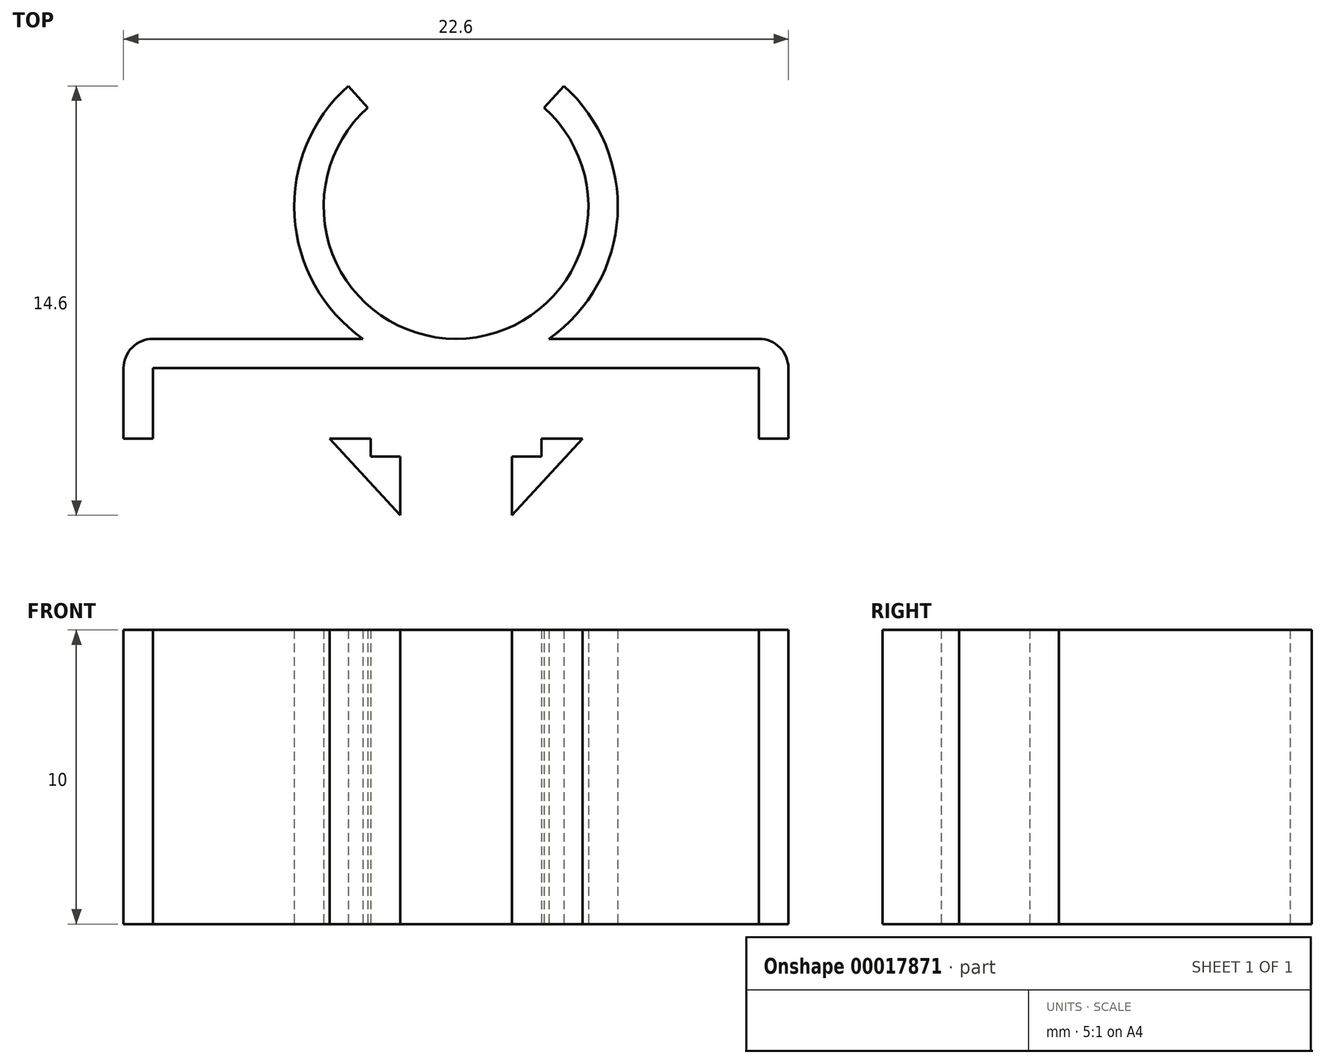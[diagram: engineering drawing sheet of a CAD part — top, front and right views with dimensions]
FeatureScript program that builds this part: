
annotation { "Feature Type Name" : "Feature", "Feature Type Description" : "" }
export const myFeature = defineFeature(function(context is Context, id is Id, definition is map)
    precondition{}
    {
        {
            var Q0;
            Q0=qCreatedBy(makeId("Top.planeOp"),FACE);
            var sketch = newSketch(context, id + "F0", { "sketchPlane" : qUnion([Q0])});
            skCircle(sketch, "E0", {"center": v(0, 0) * mm, "radius": 4.5 * mm});
            skCircle(sketch, "E1", {"center": v(0, 0) * mm, "radius": 5.5 * mm});
            skLineSegment(sketch, "E2.bottom", {"start": v(-3, 0) * mm, "end": v(3, 0) * mm});
            skLineSegment(sketch, "E2.top", {"start": v(-3, 10.18) * mm, "end": v(3, 10.18) * mm});
            skLineSegment(sketch, "E2.left", {"start": v(-3, 0) * mm, "end": v(-3, 10.18) * mm});
            skLineSegment(sketch, "E2.right", {"start": v(3, 0) * mm, "end": v(3, 10.18) * mm});
            skLineSegment(sketch, "E3.bottom", {"start": v(-10.3, -5.5) * mm, "end": v(10.3, -5.5) * mm});
            skLineSegment(sketch, "E3.top", {"start": v(-10.3, -4.5) * mm, "end": v(10.3, -4.5) * mm});
            skLineSegment(sketch, "E3.left", {"start": v(-10.3, -5.5) * mm, "end": v(-10.3, -4.5) * mm});
            skLineSegment(sketch, "E3.right", {"start": v(10.3, -5.5) * mm, "end": v(10.3, -4.5) * mm});
            skLineSegment(sketch, "E4", {"start": v(0, 0) * mm, "end": v(0, -5.5) * mm, "construction": true});
            skLineSegment(sketch, "E5", {"start": v(3, 3.35) * mm, "end": v(3.67, 4.1) * mm});
            skLineSegment(sketch, "E6", {"start": v(-3, 3.35) * mm, "end": v(-3.67, 4.1) * mm});
            skLineSegment(sketch, "E7.bottom", {"start": v(10.3, -5.5) * mm, "end": v(11.3, -5.5) * mm});
            skLineSegment(sketch, "E7.top", {"start": v(10.3, -7.9) * mm, "end": v(11.3, -7.9) * mm});
            skLineSegment(sketch, "E7.left", {"start": v(10.3, -5.5) * mm, "end": v(10.3, -7.9) * mm});
            skLineSegment(sketch, "E7.right", {"start": v(11.3, -5.5) * mm, "end": v(11.3, -7.9) * mm});
            skArc(sketch, "E8", {"start": v(11.3, -5.5) * mm, "mid": v(11, -4.8) * mm, "end": v(10.3, -4.5) * mm});
            skLineSegment(sketch, "E9.bottom", {"start": v(-10.3, -5.5) * mm, "end": v(-11.3, -5.5) * mm});
            skLineSegment(sketch, "E9.top", {"start": v(-10.3, -7.9) * mm, "end": v(-11.3, -7.9) * mm});
            skLineSegment(sketch, "E9.left", {"start": v(-10.3, -5.5) * mm, "end": v(-10.3, -7.9) * mm});
            skLineSegment(sketch, "E9.right", {"start": v(-11.3, -5.5) * mm, "end": v(-11.3, -7.9) * mm});
            skArc(sketch, "E10", {"start": v(-10.3, -4.5) * mm, "mid": v(-11, -4.8) * mm, "end": v(-11.3, -5.5) * mm});
            skLineSegment(sketch, "E11", {"start": v(-2.9, -5.5) * mm, "end": v(2.9, -5.5) * mm, "construction": true});
            skLineSegment(sketch, "E12.bottom", {"start": v(-2.9, -5.5) * mm, "end": v(-1.9, -5.5) * mm});
            skLineSegment(sketch, "E12.top", {"start": v(-2.9, -8.5) * mm, "end": v(-1.9, -8.5) * mm});
            skLineSegment(sketch, "E12.left", {"start": v(-2.9, -5.5) * mm, "end": v(-2.9, -8.5) * mm});
            skLineSegment(sketch, "E12.right", {"start": v(-1.9, -5.5) * mm, "end": v(-1.9, -8.5) * mm});
            skLineSegment(sketch, "E13.bottom", {"start": v(2.9, -5.5) * mm, "end": v(1.9, -5.5) * mm});
            skLineSegment(sketch, "E13.top", {"start": v(2.9, -8.5) * mm, "end": v(1.9, -8.5) * mm});
            skLineSegment(sketch, "E13.left", {"start": v(2.9, -5.5) * mm, "end": v(2.9, -8.5) * mm});
            skLineSegment(sketch, "E13.right", {"start": v(1.9, -5.5) * mm, "end": v(1.9, -8.5) * mm});
            skLineSegment(sketch, "E14", {"start": v(4.3, -7.9) * mm, "end": v(2.9, -7.9) * mm});
            skLineSegment(sketch, "E15", {"start": v(-2.9, -7.9) * mm, "end": v(-4.3, -7.9) * mm});
            skLineSegment(sketch, "E16", {"start": v(-2.9, -7.9) * mm, "end": v(2.9, -7.9) * mm, "construction": true});
            skLineSegment(sketch, "E17", {"start": v(1.9, -8.5) * mm, "end": v(1.9, -10.5) * mm});
            skLineSegment(sketch, "E18", {"start": v(1.9, -10.5) * mm, "end": v(4.3, -7.9) * mm});
            skLineSegment(sketch, "E19", {"start": v(-1.9, -8.5) * mm, "end": v(-1.9, -10.5) * mm});
            skLineSegment(sketch, "E20", {"start": v(-1.9, -10.5) * mm, "end": v(-4.3, -7.9) * mm});
            skSolve(sketch);
        }
        {
            var Q0;
            Q0=makeQuery(id+"F0.imprint","IMPRINT",FACE,{"disambiguationData":[TD([[makeQuery(id+"F0.imprint","IMPRINT",EDGE,{"derivedFrom":sQuery(id+"F0.wireOp",EDGE,"E7.bottom")}),-1.0]])]});
            var Q1;
            Q1=makeQuery(id+"F0.imprint","IMPRINT",FACE,{"disambiguationData":[TD([[makeQuery(id+"F0.imprint","IMPRINT",EDGE,{"derivedFrom":sQuery(id+"F0.wireOp",EDGE,"E9.bottom")}),1.0]])]});
            var Q2;
            {var subQ1=sQuery(id+"F0.wireOp",EDGE,"E15");Q2=makeQuery(id+"F0.imprint","IMPRINT",FACE,{"disambiguationData":[TD([[makeQuery(id+"F0.imprint","IMPRINT",EDGE,{"derivedFrom":subQ1}),1.0]])]});}
            var Q3;
            {var subQ1=sQuery(id+"F0.wireOp",EDGE,"7c9eb7b9-ca48-4d36-bab2-391d59fa54ff");Q3=makeQuery(id+"F0.imprint","IMPRINT",FACE,{"disambiguationData":[TD([[makeQuery(id+"F0.imprint","IMPRINT",EDGE,{"derivedFrom":subQ1}),-1.0]])]});}
            var Q4;
            Q4=makeQuery(id+"F0.imprint","IMPRINT",FACE,{"disambiguationData":[TD([[makeQuery(id+"F0.imprint","IMPRINT",EDGE,{"derivedFrom":sQuery(id+"F0.wireOp",EDGE,"E3.left")}),1.0]])]});
            var Q5;
            Q5=makeQuery(id+"F0.imprint","IMPRINT",FACE,{"disambiguationData":[TD([[makeQuery(id+"F0.imprint","IMPRINT",EDGE,{"derivedFrom":sQuery(id+"F0.wireOp",EDGE,"E3.right")}),-1.0]])]});
            var Q6;
            {var subQ3=sQuery(id+"F0.wireOp",EDGE,"E12.bottom");Q6=makeQuery(id+"F0.imprint","IMPRINT",FACE,{"disambiguationData":[TD([[makeQuery(id+"F0.imprint","IMPRINT",EDGE,{"derivedFrom":subQ3}),-1.0]])]});}
            var Q7;
            {var subQ2=sQuery(id+"F0.wireOp",EDGE,"E13.bottom");Q7=makeQuery(id+"F0.imprint","IMPRINT",FACE,{"disambiguationData":[TD([[makeQuery(id+"F0.imprint","IMPRINT",EDGE,{"derivedFrom":subQ2}),1.0]])]});}
            var Q8;
            {var subQ0=sQuery(id+"F0.wireOp",EDGE,"E6");Q8=makeQuery(id+"F0.imprint","IMPRINT",FACE,{"disambiguationData":[TD([[makeQuery(id+"F0.imprint","IMPRINT",EDGE,{"derivedFrom":subQ0}),1.0]])]});}
            var Q9;
            {var subQ0=sQuery(id+"F0.wireOp",EDGE,"E5");Q9=makeQuery(id+"F0.imprint","IMPRINT",FACE,{"disambiguationData":[TD([[makeQuery(id+"F0.imprint","IMPRINT",EDGE,{"derivedFrom":subQ0}),-1.0]])]});}
            var Q10;
            {var subQ1=sQuery(id+"F0.wireOp",EDGE,"E3.left");Q10=makeQuery(id+"F0.imprint","IMPRINT",FACE,{"disambiguationData":[TD([[makeQuery(id+"F0.imprint","IMPRINT",EDGE,{"derivedFrom":subQ1}),-1.0]])]});}
            var Q11;
            {var subQ1=sQuery(id+"F0.wireOp",EDGE,"E3.right");Q11=makeQuery(id+"F0.imprint","IMPRINT",FACE,{"disambiguationData":[TD([[makeQuery(id+"F0.imprint","IMPRINT",EDGE,{"derivedFrom":subQ1}),1.0]])]});}
            var Q12;
            {var subQ0=sQuery(id+"F0.wireOp",EDGE,"E3.top");var subQ2=sQuery(id+"F0.wireOp",EDGE,"E1");var subQ4=makeQuery(id+"F0.imprint","INTERSECT",VERTEX,{"disambiguationData":[OD(0.0)],"derivedFrom":[subQ2,subQ0]});Q12=makeQuery(id+"F0.imprint","IMPRINT",FACE,{"disambiguationData":[TD([[makeQuery(id+"F0.imprint","IMPRINT",EDGE,{"disambiguationData":[TD([[subQ4,-1.0]])],"derivedFrom":subQ2}),1.0]])]});}
            var Q13;
            {var subQ2=sQuery(id+"F0.wireOp",EDGE,"E13.top");Q13=makeQuery(id+"F0.imprint","IMPRINT",FACE,{"disambiguationData":[TD([[makeQuery(id+"F0.imprint","IMPRINT",EDGE,{"derivedFrom":subQ2}),1.0]])]});}
            extrude(context, id + "F1", {"entities" : qUnion([Q0, Q1, Q2, Q3, Q4, Q5, Q6, Q7, Q8, Q9, Q10, Q11, Q12, Q13]), "depth" : 10 * mm});
        }
    });
